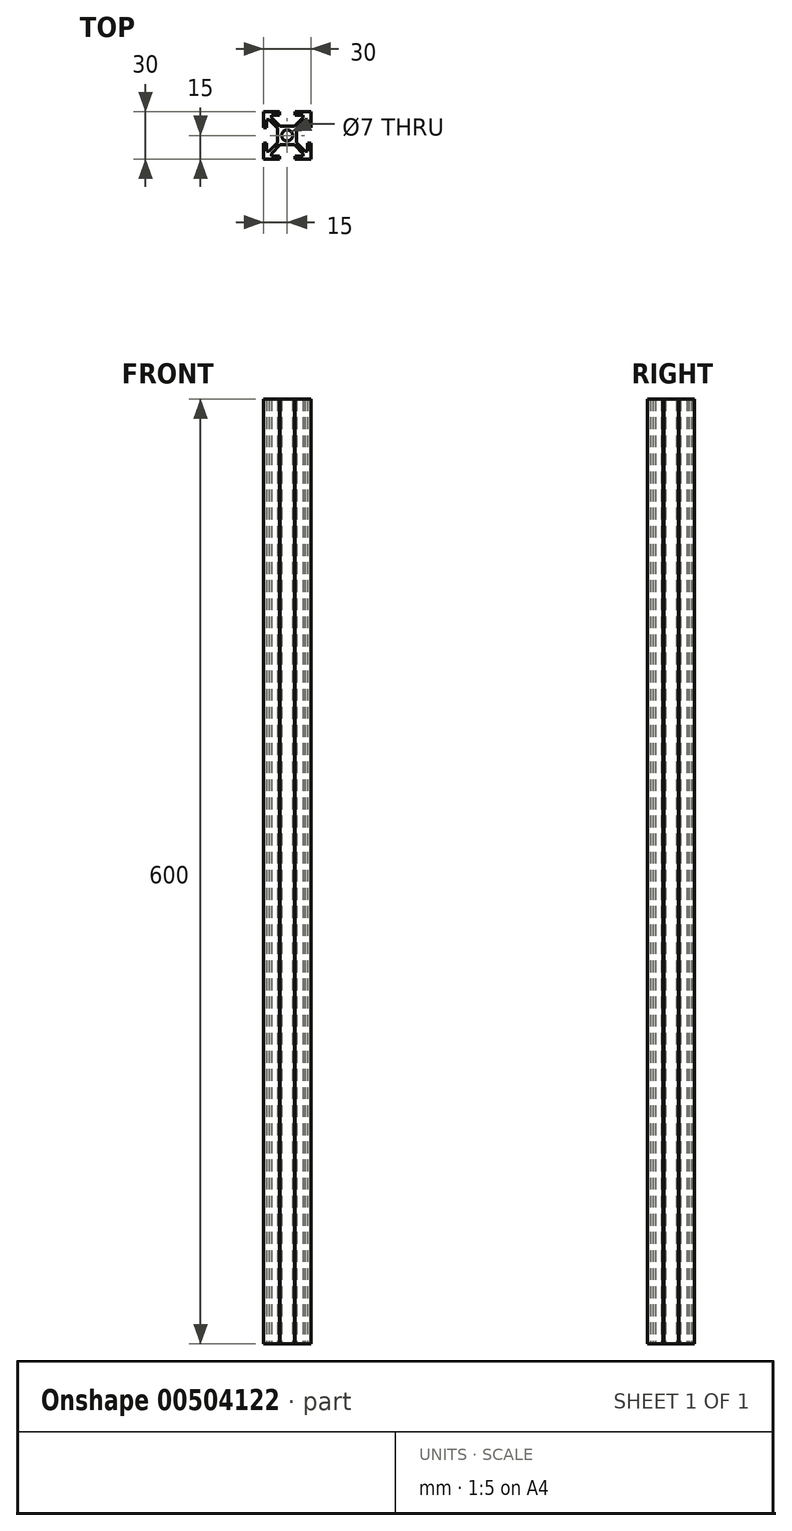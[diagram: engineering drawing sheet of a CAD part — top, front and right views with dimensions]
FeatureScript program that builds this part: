
annotation { "Feature Type Name" : "Feature", "Feature Type Description" : "" }
export const myFeature = defineFeature(function(context is Context, id is Id, definition is map)
    precondition{}
    {
        {
            var Q0;
            Q0=qCreatedBy(makeId("Top.planeOp"),FACE);
            var sketch = newSketch(context, id + "F0", { "sketchPlane" : qUnion([Q0])});
            skCircle(sketch, "E0", {"center": v(0, 0) * mm, "radius": 3.5 * mm});
            skLineSegment(sketch, "E1.bottom", {"start": v(-4.59, 6) * mm, "end": v(4.59, 6) * mm});
            skLineSegment(sketch, "E1.top", {"start": v(-4.59, -6) * mm, "end": v(4.59, -6) * mm});
            skLineSegment(sketch, "E1.left", {"start": v(-6, 4.59) * mm, "end": v(-6, -4.59) * mm});
            skLineSegment(sketch, "E1.right", {"start": v(6, 4.59) * mm, "end": v(6, -4.59) * mm});
            skLineSegment(sketch, "E2", {"start": v(-6, 4.59) * mm, "end": v(-11.41, 10) * mm});
            skLineSegment(sketch, "E3", {"start": v(-4.59, 6) * mm, "end": v(-10, 11.41) * mm});
            skLineSegment(sketch, "E4", {"start": v(-11.41, 10) * mm, "end": v(-13, 10) * mm});
            skLineSegment(sketch, "E5", {"start": v(-13, 10) * mm, "end": v(-13, 5) * mm});
            skLineSegment(sketch, "E6", {"start": v(-13, 5) * mm, "end": v(-15, 5) * mm});
            skLineSegment(sketch, "E7", {"start": v(-15, 5) * mm, "end": v(-15, 15) * mm});
            skLineSegment(sketch, "E8", {"start": v(-15, 15) * mm, "end": v(-5, 15) * mm});
            skLineSegment(sketch, "E9", {"start": v(-5, 15) * mm, "end": v(-5, 13) * mm});
            skLineSegment(sketch, "E10", {"start": v(-5, 13) * mm, "end": v(-10, 13) * mm});
            skLineSegment(sketch, "E11", {"start": v(-10, 13) * mm, "end": v(-10, 11.41) * mm});
            skPoint(sketch, "E12.orphan", {"position": v(-6, 6) * mm});
            skLineSegment(sketch, "E13", {"start": v(0, 0) * mm, "end": v(-5.3, 5.3) * mm, "construction": true});
            skLineSegment(sketch, "E14", {"start": v(-5.3, 5.3) * mm, "end": v(-6, 4.59) * mm, "construction": true});
            skLineSegment(sketch, "E15", {"start": v(-5.3, 5.3) * mm, "end": v(-4.59, 6) * mm, "construction": true});
            skLineSegment(sketch, "E16.2.0", {"start": v(15, 15) * mm, "end": v(15, 5) * mm});
            skLineSegment(sketch, "E16.2.1", {"start": v(5, 15) * mm, "end": v(15, 15) * mm});
            skLineSegment(sketch, "E16.2.2", {"start": v(5, 13) * mm, "end": v(5, 15) * mm});
            skLineSegment(sketch, "E16.2.3", {"start": v(10, 13) * mm, "end": v(5, 13) * mm});
            skLineSegment(sketch, "E16.2.4", {"start": v(10, 11.41) * mm, "end": v(10, 13) * mm});
            skLineSegment(sketch, "E16.2.5", {"start": v(4.59, 6) * mm, "end": v(10, 11.41) * mm});
            skLineSegment(sketch, "E16.2.6", {"start": v(6, 4.59) * mm, "end": v(11.41, 10) * mm});
            skLineSegment(sketch, "E16.2.7", {"start": v(13, 10) * mm, "end": v(11.41, 10) * mm});
            skLineSegment(sketch, "E16.2.8", {"start": v(13, 5) * mm, "end": v(13, 10) * mm});
            skLineSegment(sketch, "E16.2.9", {"start": v(15, 5) * mm, "end": v(13, 5) * mm});
            skLineSegment(sketch, "E16.anchor1", {"start": v(0, 0) * mm, "end": v(-15, 15) * mm, "construction": true});
            skLineSegment(sketch, "E16.anchor2", {"start": v(0, 0) * mm, "end": v(15, 15) * mm, "construction": true});
            skPoint(sketch, "E17.orphan", {"position": v(6, 6) * mm});
            skLineSegment(sketch, "E18.MirrorCS", {"start": v(-13, -5) * mm, "end": v(-15, -5) * mm});
            skLineSegment(sketch, "E19.MirrorCS", {"start": v(-15, -5) * mm, "end": v(-15, -15) * mm});
            skLineSegment(sketch, "E20.MirrorCS", {"start": v(-13, -10) * mm, "end": v(-13, -5) * mm});
            skLineSegment(sketch, "E21.MirrorCS", {"start": v(-11.41, -10) * mm, "end": v(-13, -10) * mm});
            skLineSegment(sketch, "E22.MirrorCS", {"start": v(-6, -4.59) * mm, "end": v(-11.41, -10) * mm});
            skLineSegment(sketch, "E23.MirrorCS", {"start": v(-4.59, -6) * mm, "end": v(-10, -11.41) * mm});
            skLineSegment(sketch, "E24.MirrorCS", {"start": v(-5, -13) * mm, "end": v(-10, -13) * mm});
            skLineSegment(sketch, "E25.MirrorCS", {"start": v(-10, -13) * mm, "end": v(-10, -11.41) * mm});
            skLineSegment(sketch, "E26.MirrorCS", {"start": v(-5, -15) * mm, "end": v(-5, -13) * mm});
            skLineSegment(sketch, "E27.MirrorCS", {"start": v(-15, -15) * mm, "end": v(-5, -15) * mm});
            skLineSegment(sketch, "E28.MirrorCS", {"start": v(5, -13) * mm, "end": v(5, -15) * mm});
            skLineSegment(sketch, "E29.MirrorCS", {"start": v(5, -15) * mm, "end": v(15, -15) * mm});
            skLineSegment(sketch, "E30.MirrorCS", {"start": v(15, -15) * mm, "end": v(15, -5) * mm});
            skLineSegment(sketch, "E31.MirrorCS", {"start": v(15, -5) * mm, "end": v(13, -5) * mm});
            skLineSegment(sketch, "E32.MirrorCS", {"start": v(13, -5) * mm, "end": v(13, -10) * mm});
            skLineSegment(sketch, "E33.MirrorCS", {"start": v(13, -10) * mm, "end": v(11.41, -10) * mm});
            skLineSegment(sketch, "E34.MirrorCS", {"start": v(6, -4.59) * mm, "end": v(11.41, -10) * mm});
            skLineSegment(sketch, "E35.MirrorCS", {"start": v(4.59, -6) * mm, "end": v(10, -11.41) * mm});
            skLineSegment(sketch, "E36.MirrorCS", {"start": v(10, -13) * mm, "end": v(5, -13) * mm});
            skLineSegment(sketch, "E37.MirrorCS", {"start": v(10, -11.41) * mm, "end": v(10, -13) * mm});
            skPoint(sketch, "E38.orphan", {"position": v(-6, -6) * mm});
            skPoint(sketch, "E39.orphan", {"position": v(6, -6) * mm});
            skSolve(sketch);
        }
        {
            var Q0;
            Q0=qSketchRegion(id+"F0",true);
            extrude(context, id + "F1", {"entities" : qUnion([Q0]), "depth" : 600 * mm});
        }
    });
